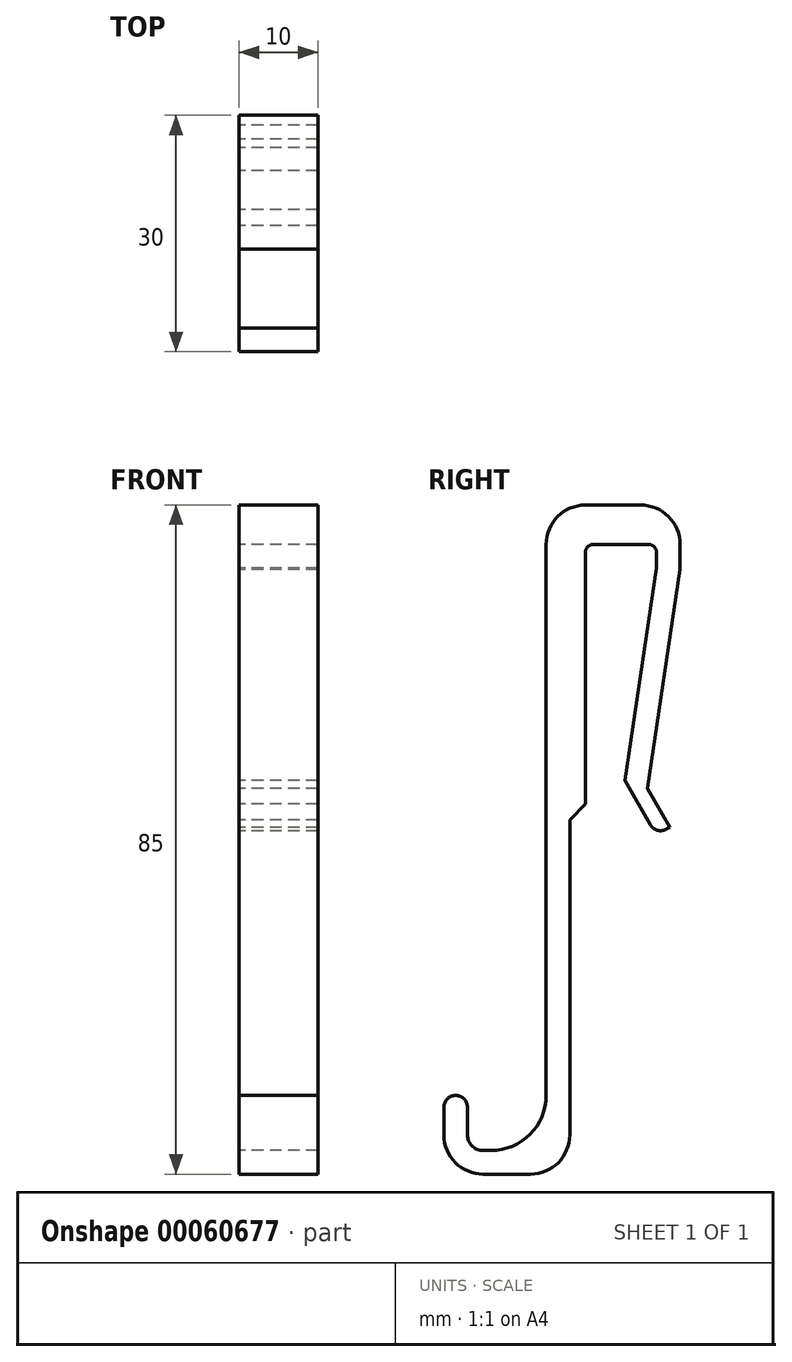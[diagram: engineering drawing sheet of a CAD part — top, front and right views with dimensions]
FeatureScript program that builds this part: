
annotation { "Feature Type Name" : "Feature", "Feature Type Description" : "" }
export const myFeature = defineFeature(function(context is Context, id is Id, definition is map)
    precondition{}
    {
        {
            var Q0;
            Q0=qCreatedBy(makeId("Right.planeOp"),FACE);
            var sketch = newSketch(context, id + "F0", { "sketchPlane" : qUnion([Q0])});
            skLineSegment(sketch, "E0", {"start": v(0, 0) * mm, "end": v(9, 0) * mm});
            skLineSegment(sketch, "E1", {"start": v(9, 0) * mm, "end": v(9, -3) * mm});
            skLineSegment(sketch, "E2", {"start": v(9, -3) * mm, "end": v(5, -30) * mm});
            skLineSegment(sketch, "E3", {"start": v(5, -30) * mm, "end": v(9, -36.93) * mm});
            skLineSegment(sketch, "E4", {"start": v(9, -36.93) * mm, "end": v(10.73, -35.93) * mm});
            skLineSegment(sketch, "E5", {"start": v(10.73, -35.93) * mm, "end": v(7.89, -31) * mm});
            skLineSegment(sketch, "E6", {"start": v(7.89, -31) * mm, "end": v(12, -3.22) * mm});
            skLineSegment(sketch, "E7", {"start": v(12, -3.22) * mm, "end": v(12, 5) * mm});
            skLineSegment(sketch, "E8", {"start": v(12, 5) * mm, "end": v(-5, 5) * mm});
            skLineSegment(sketch, "E9", {"start": v(-5, 5) * mm, "end": v(-5, -77) * mm});
            skLineSegment(sketch, "E10", {"start": v(-2, -80) * mm, "end": v(-2, -35) * mm});
            skLineSegment(sketch, "E11", {"start": v(-2, -35) * mm, "end": v(0, -35) * mm});
            skLineSegment(sketch, "E12", {"start": v(0, -35) * mm, "end": v(0, 0) * mm});
            skLineSegment(sketch, "E13", {"start": v(-5, -77) * mm, "end": v(-15, -77) * mm});
            skLineSegment(sketch, "E14", {"start": v(-15, -77) * mm, "end": v(-15, -70) * mm});
            skLineSegment(sketch, "E15", {"start": v(-15, -70) * mm, "end": v(-18, -70) * mm});
            skLineSegment(sketch, "E16", {"start": v(-18, -70) * mm, "end": v(-18, -80) * mm});
            skLineSegment(sketch, "E17", {"start": v(-18, -80) * mm, "end": v(-2, -80) * mm});
            skLineSegment(sketch, "E18", {"start": v(9, 0) * mm, "end": v(12, 0) * mm, "construction": true});
            skLineSegment(sketch, "E19", {"start": v(7, -16.5) * mm, "end": v(9.97, -16.94) * mm, "construction": true});
            skSolve(sketch);
        }
        {
            var Q0;
            Q0=qSketchRegion(id+"F0",true);
            extrude(context, id + "F1", {"entities" : qUnion([Q0]), "depth" : 10 * mm});
        }
        {
            var Q0;
            Q0=makeQuery(id+"F1.opExtrude","SWEPT_EDGE",EDGE,{"disambiguationData":[OSD([sQuery(id+"F0.wireOp",EDGE,"E9"),sQuery(id+"F0.wireOp",EDGE,"E13")])]});
            fillet(context, id + "F2", {"entities" : qUnion([Q0]), "radius" : 7 * mm, "tangentPropagation" : true, "allowEdgeOverflow" : false});
        }
        {
            var Q0;
            Q0=makeQuery(id+"F1.opExtrude","SWEPT_EDGE",EDGE,{"disambiguationData":[OSD([sQuery(id+"F0.wireOp",EDGE,"E13"),sQuery(id+"F0.wireOp",EDGE,"E14")])]});
            fillet(context, id + "F3", {"entities" : qUnion([Q0]), "radius" : 2 * mm, "tangentPropagation" : true, "allowEdgeOverflow" : false});
        }
        {
            var Q0;
            Q0=makeQuery(id+"F1.opExtrude","SWEPT_EDGE",EDGE,{"disambiguationData":[OSD([sQuery(id+"F0.wireOp",EDGE,"E17"),sQuery(id+"F0.wireOp",EDGE,"zfrpbxgG-opix-UUFs-7G0M-IxrEZ5RHV5OJ")])]});
            var Q1;
            Q1=makeQuery(id+"F1.opExtrude","SWEPT_EDGE",EDGE,{"disambiguationData":[OSD([sQuery(id+"F0.wireOp",EDGE,"E8"),sQuery(id+"F0.wireOp",EDGE,"E9")])]});
            var Q2;
            Q2=makeQuery(id+"F1.opExtrude","SWEPT_EDGE",EDGE,{"disambiguationData":[OSD([sQuery(id+"F0.wireOp",EDGE,"E7"),sQuery(id+"F0.wireOp",EDGE,"E8")])]});
            fillet(context, id + "F4", {"entities" : qUnion([Q0, Q1, Q2]), "radius" : 5 * mm, "tangentPropagation" : true, "allowEdgeOverflow" : false});
        }
        {
            var Q0;
            Q0=makeQuery(id+"F1.opExtrude","SWEPT_EDGE",EDGE,{"disambiguationData":[OSD([sQuery(id+"F0.wireOp",EDGE,"E3"),sQuery(id+"F0.wireOp",EDGE,"E4")])]});
            var Q1;
            Q1=makeQuery(id+"F1.opExtrude","SWEPT_EDGE",EDGE,{"disambiguationData":[OSD([sQuery(id+"F0.wireOp",EDGE,"E16"),sQuery(id+"F0.wireOp",EDGE,"E17")])]});
            var Q2;
            Q2=makeQuery(id+"F1.opExtrude","SWEPT_EDGE",EDGE,{"disambiguationData":[OSD([sQuery(id+"F0.wireOp",EDGE,"E15"),sQuery(id+"F0.wireOp",EDGE,"E16")])]});
            var Q3;
            Q3=makeQuery(id+"F1.opExtrude","SWEPT_EDGE",EDGE,{"disambiguationData":[OSD([sQuery(id+"F0.wireOp",EDGE,"E14"),sQuery(id+"F0.wireOp",EDGE,"E15")])]});
            fillet(context, id + "F5", {"entities" : qUnion([Q0, Q1, Q2, Q3]), "radius" : 1.5 * mm, "tangentPropagation" : true, "allowEdgeOverflow" : false});
        }
        {
            var Q0;
            Q0=makeQuery(id+"F1.opExtrude","SWEPT_EDGE",EDGE,{"disambiguationData":[OSD([sQuery(id+"F0.wireOp",EDGE,"E11"),sQuery(id+"F0.wireOp",EDGE,"E12")])]});
            chamfer(context, id + "F6", {"entities" : qUnion([Q0]), "width" : 2 * mm, "tangentPropagation" : true});
        }
        {
            var Q0;
            Q0=makeQuery(id+"F1.opExtrude","SWEPT_EDGE",EDGE,{"disambiguationData":[OSD([sQuery(id+"F0.wireOp",EDGE,"E0"),sQuery(id+"F0.wireOp",EDGE,"E12")])]});
            var Q1;
            Q1=makeQuery(id+"F1.opExtrude","SWEPT_EDGE",EDGE,{"disambiguationData":[OSD([sQuery(id+"F0.wireOp",EDGE,"E0"),sQuery(id+"F0.wireOp",EDGE,"E1")])]});
            fillet(context, id + "F7", {"entities" : qUnion([Q0, Q1]), "radius" : 1 * mm, "tangentPropagation" : true, "allowEdgeOverflow" : false});
        }
    });
